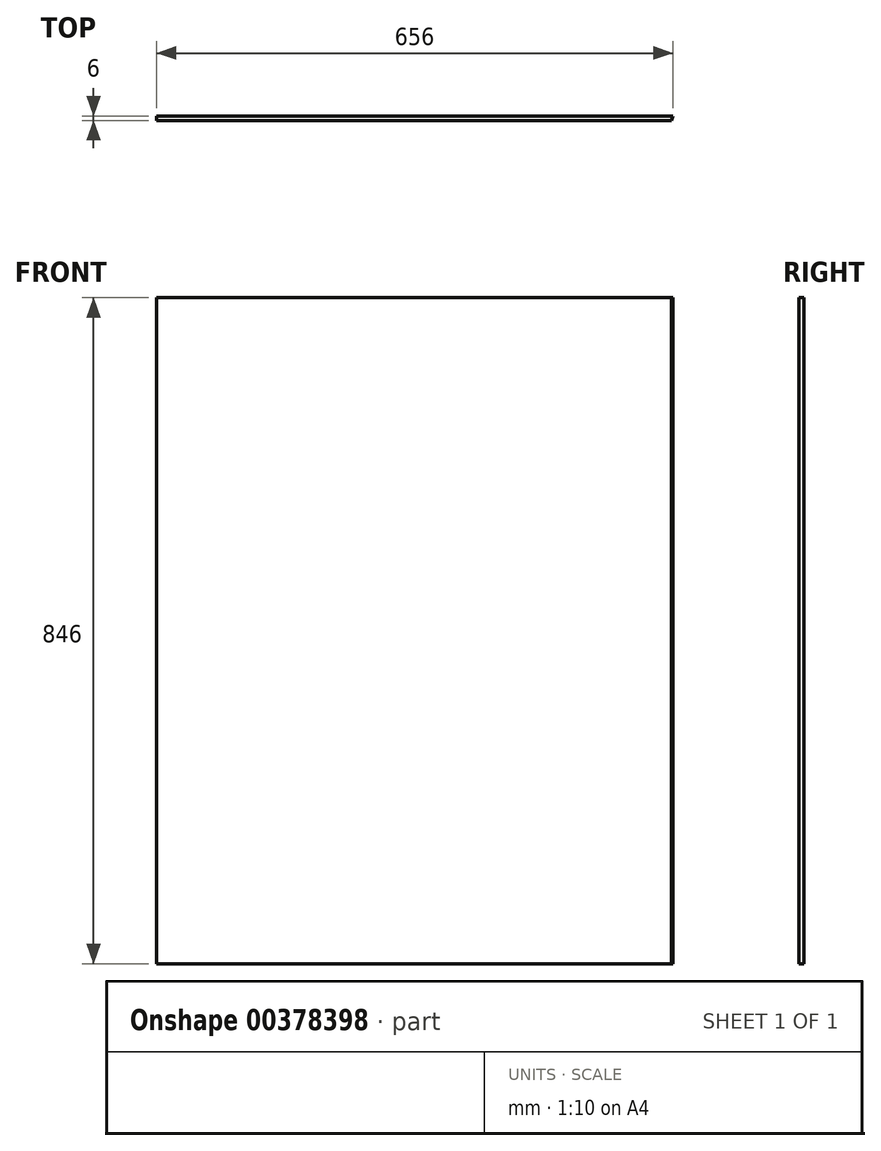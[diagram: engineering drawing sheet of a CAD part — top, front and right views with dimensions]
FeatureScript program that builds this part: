
annotation { "Feature Type Name" : "Feature", "Feature Type Description" : "" }
export const myFeature = defineFeature(function(context is Context, id is Id, definition is map)
    precondition{}
    {
        {
            var Q0;
            Q0=qCreatedBy(makeId("Front.planeOp"),FACE);
            var sketch = newSketch(context, id + "F0", { "sketchPlane" : qUnion([Q0])});
            skLineSegment(sketch, "E0.bottom", {"start": v(328, 423) * mm, "end": v(-328, 423) * mm});
            skLineSegment(sketch, "E0.top", {"start": v(328, -423) * mm, "end": v(-328, -423) * mm});
            skLineSegment(sketch, "E0.left", {"start": v(328, 423) * mm, "end": v(328, -423) * mm});
            skLineSegment(sketch, "E0.right", {"start": v(-328, 423) * mm, "end": v(-328, -423) * mm});
            skPoint(sketch, "E0.middle", {"position": v(0, 0) * mm});
            skSolve(sketch);
        }
        {
            var Q0;
            Q0 = qSketchRegion(id + "F0", true);
            extrude(context, id + "F1", {"entities" : qUnion([Q0]), "depth" : 6 * mm});
        }
        {
            var Q0;
            Q0=makeQuery(id+"F1.opExtrude","SWEPT_FACE",FACE,{"disambiguationData":[OSD([sQuery(id+"F0.wireOp",EDGE,"E0.bottom")])]});
            var sketch = newSketch(context, id + "F2", { "sketchPlane" : qUnion([Q0])});
            skLineSegment(sketch, "E1", {"start": v(328, -6) * mm, "end": v(328, 0) * mm});
            skLineSegment(sketch, "E2", {"start": v(328, 0) * mm, "end": v(325.7, -6) * mm});
            skLineSegment(sketch, "E3", {"start": v(325.7, -6) * mm, "end": v(328, -6) * mm});
            skSolve(sketch);
        }
        {
            var Q0;
            Q0 = qSketchRegion(id + "F2", true);
            extrude(context, id + "F3", {"entities" : qUnion([Q0]), "operationType" : NewBodyOperationType.REMOVE, "oppositeDirection" : true, "depth" : 870 * mm});
        }
    });
